# Revit family: HL_Dachablauf_HL64H-B-221103
name_source: partatom
category: Instalační zařizovací předměty
units: mm (PartAtom-declared; Revit-internal decimal feet)

## family parameters
Bod výpočtu místnosti = Ano
Kóta kulaté spojky = Použít průměr
Nadpis OmniClass = Deck Waste Water Drains
Ořezat dutým tvarem při načtení = Ne
Sdílené = Ne
Typ dílu = Normální
Vždy vertikální = Ano
Založené na pracovní rovině = Ne
Číslo OmniClass = 23.70.50.21.24.14

## types (1)
- HL_Dachablauf_HL64H
    DIMENSION = DN75/110
    EAN = 9003076801640
    EINBAUHÖHE = 147 mm
    EINLAUFROST = Laubfangkorb d 145 mm
    GEWICHT = 1,95 [kg]
    Indexovaná poznámka = HL64H
    Komentáře k typům = HL64H Dachablauf DN75/110 waagrecht mit Bitumenmanschette,
    LEISTUNG = DN75 = 10,0l/s; DN110 = 6,0l/s
    MATERIAL = PP
    Model = HL64H
    Popis = Dachabläufe
    Přípoj CW = Ne
    Přípoj HW = Ne
    Přípoj odpadních dílů = Ano
    Přípoj ventilace = Ne
    URL = http://www.hutterer-lechner.com
    Výchozí výška = 0 mm  [stored 0 ft]
    Výrobce = HL Hutterer & Lechner GmbH

note: [stored X ft] marks values corroborated as IEEE doubles in the binary element streams (Revit-internal decimal feet)

## geometry (parser evidence)
native form markers: Sweep x16
no freeform markers — native parametric forms only
